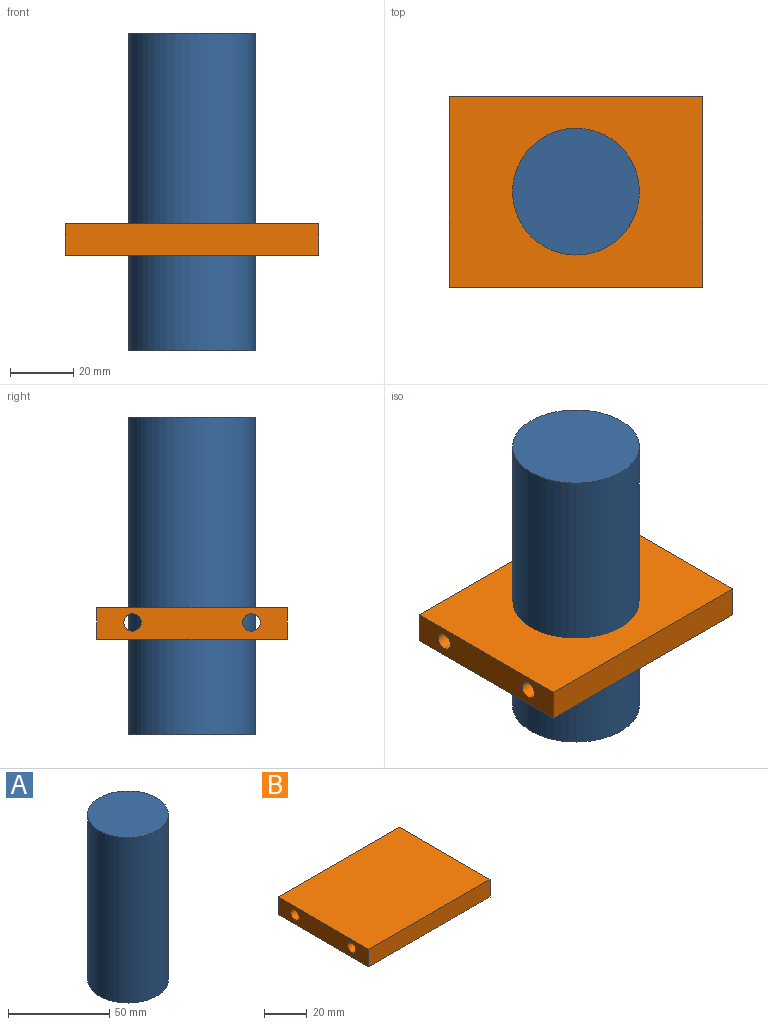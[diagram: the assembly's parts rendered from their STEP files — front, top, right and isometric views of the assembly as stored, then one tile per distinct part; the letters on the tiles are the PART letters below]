
ASSEMBLY  parts=2 mates=1
PART A: 3 faces, bbox 40x40x100 mm
  f0: cylinder r=20mm len=100mm, axis (0,0,-1), area 12566.4mm2, adj f1,f2
  f1: plane 40x40mm, normal (0,0,1), area 1256.6mm2, adj f0
  f2: plane 40x40mm, normal (0,0,-1), area 1256.6mm2, adj f0
PART B: 8 faces, bbox 80x60x10 mm
  f0: plane 80x10mm, normal (0,-1,0), area 800mm2, adj f1,f3,f4,f5
  f1: plane 60x10mm, normal (1,0,0), area 552.5mm2, adj f0,f2,f4,f5,f6,f7
  f2: plane 80x10mm, normal (0,1,0), area 800mm2, adj f1,f3,f4,f5
  f3: plane 60x10mm, normal (-1,0,0), area 552.5mm2, adj f0,f2,f4,f5,f6,f7
  f4: plane 80x60mm, normal (0,0,1), area 4800mm2, adj f0,f1,f2,f3
  f5: plane 80x60mm, normal (0,0,-1), area 4800mm2, adj f0,f1,f2,f3
  f6: cylinder r=2.75mm len=80mm, axis (1,0,0), area 1382.3mm2, adj f1,f3
  f7: cylinder r=2.75mm len=80mm, axis (1,0,0), area 1382.3mm2, adj f1,f3
PLACE A t=(0,0,50)mm
PLACE B t=(0,0,30)mm
MATE slider B.f4 <-> A.f0  axis (0,0,1) through (0,0,40)mm
